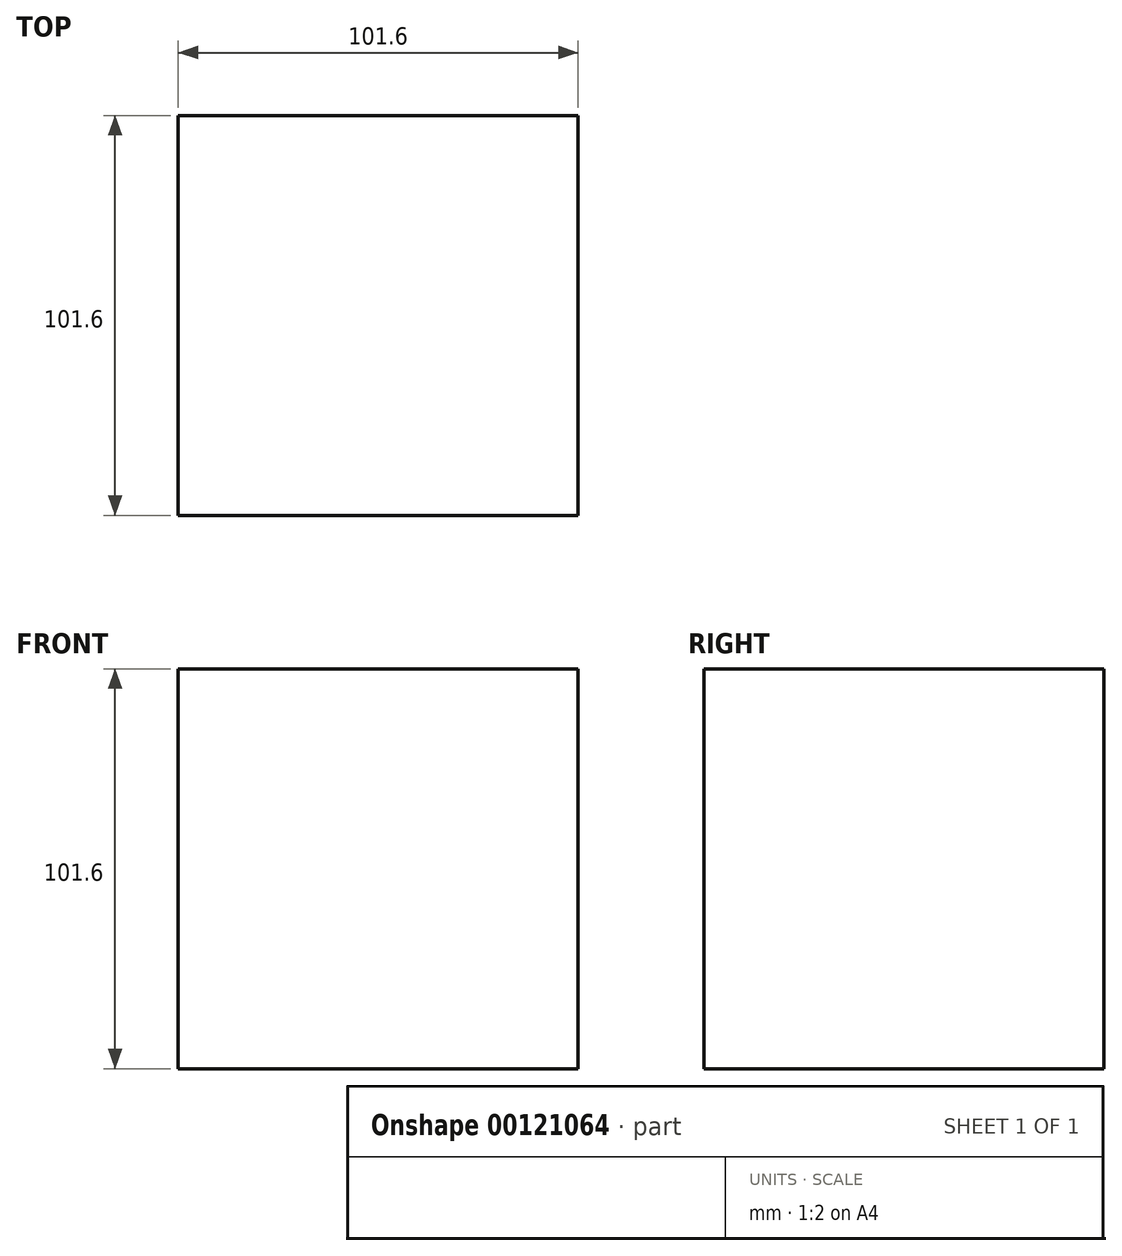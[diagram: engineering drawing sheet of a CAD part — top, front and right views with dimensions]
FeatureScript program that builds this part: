
annotation { "Feature Type Name" : "Feature", "Feature Type Description" : "" }
export const myFeature = defineFeature(function(context is Context, id is Id, definition is map)
    precondition{}
    {
        {
            var Q0;
            Q0=qCreatedBy(makeId("Top.planeOp"),FACE);
            var sketch = newSketch(context, id + "F0", { "sketchPlane" : qUnion([Q0])});
            skLineSegment(sketch, "E0.bottom", {"start": v(-50.8, 50.8) * mm, "end": v(50.8, 50.8) * mm});
            skLineSegment(sketch, "E0.top", {"start": v(-50.8, -50.8) * mm, "end": v(50.8, -50.8) * mm});
            skLineSegment(sketch, "E0.left", {"start": v(-50.8, 50.8) * mm, "end": v(-50.8, -50.8) * mm});
            skLineSegment(sketch, "E0.right", {"start": v(50.8, 50.8) * mm, "end": v(50.8, -50.8) * mm});
            skPoint(sketch, "E0.middle", {"position": v(0, 0) * mm});
            skSolve(sketch);
        }
        {
            var Q0;
            Q0 = qSketchRegion(id + "F0", true);
            extrude(context, id + "F1", {"entities" : qUnion([Q0]), "depth" : 101.6 * mm});
        }
    });
